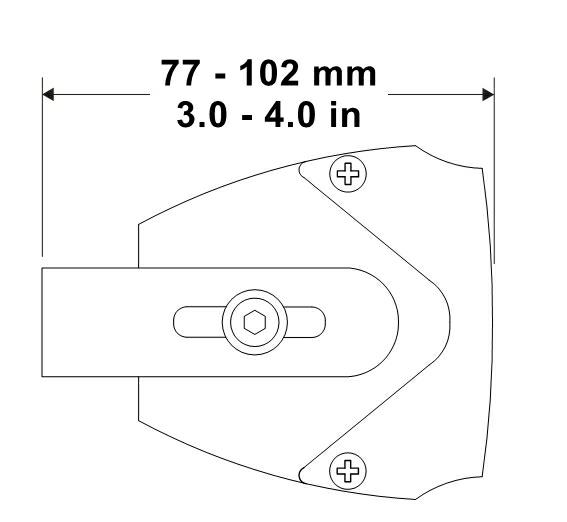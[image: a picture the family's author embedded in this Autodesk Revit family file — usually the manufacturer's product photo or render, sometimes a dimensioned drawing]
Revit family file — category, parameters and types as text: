
# Revit family: Electronics_Desono_Biamp_Two-Way-Column-Loudspeaker_COLS101
name_source: partatom
category: Communication Devices
units: mm (PartAtom-declared; Revit-internal decimal feet)

## family parameters
Cut with Voids When Loaded = No
Host = Face
Maintain Annotation Orientation = No
OmniClass Number = 23.85.10.11.14.14.14
OmniClass Title = Loudspeakers
Part Type = Normal
Room Calculation Point = No
Round Connector Dimension = Use Diameter
Shared = No

## types (1)
- COLS101
    Bracket Material = Biamp - Metal - White
    Connector Description = Terminal block; Low impedance 16 ohms; 70V/100V operation
    Continuous Power Handling Nominal Impedance = 15V; 30W @ 8Ω (120W peak)
    Controls = None; select transformer tap or low impedance input via terminal block wiring
    Default Elevation = 4' - 0"
    Depth = 0' - 2 1/2"
    Description = Desono™ COLS101 Two-Way 10 x 2 Column Loudspeaker
    Environmental = IP66 per IEC 60529
    Grill Material = Biamp - Plastic - White(Grid)
    Height = 2' - 4 1/2"
    Housing Material = Biamp - Plastic - White
    Input Connection = Multi-position pass-through, screw-down terminal block
    Manufacturer = Biamp
    Model = COLS101
    Mounting Provisions = Adjustable tilt L-bracket
    Nominal Beamwidth (H x V) = 120° x 10°
    Nominal Maximum SPL @ 1m = Peak - 112dB; Continuous - 106dB
    Nominal Sensitivity @ 1m = 1W - 91dB; 2.83V - 91dB
    Operating Environment = Indoor/Outdoor
    Operating Mode = Passive
    Operating Range 2 (-10dB) = 195 Hz to 22 kHz
    Product Documentation Link = https://downloads.biamp.com
    Product Page URL = https://www.biamp.com
    Product data url = https://www.bimobject.com
    Recommended Amplifers = 30W - 60W @ 8Ω (20V - 28V)
    Shipping Weight = 8.60 lb
    Transducers = LF 10 x 2 (51 mm) coated paper cone HF 1 x 1 (25 mm) soft dome
    Transformer = 70V: 40W, 20W, 10W, 5W; 100V: 40W, 20W, 10W
    URL = https://www.biamp.com
    Weight = 7.30 lb
    Width = 0' - 2 1/2"

## geometry (parser evidence)
native form markers: Sweep x5
no freeform markers — native parametric forms only
